# Revit family: 01546283
name_source: partatom
category: Plumbing Fixtures
revit_build: Autodesk Revit 2018 (Build: 20170223_1515(x64)
units: mm (PartAtom-declared; Revit-internal decimal feet)

## family parameters
Always vertical = Yes
Cut with Voids When Loaded = No
OmniClass Number = 23.45.55.00
OmniClass Title = Sanitary Faucets, Wastes
Part Type = Normal
Room Calculation Point = No
Round Connector Dimension = Use Diameter
Shared = No
Work Plane-Based = No

## types (1)
- 01546283 Washbasin faucet
    2D/3D/BIM Files URL = http://static.hansa.com
    3D View = https://static.hansa.com
    Advanced Features = Inner body made of DZR brass;Waterways without nickel coating
    Aerator = Laminar stream
    Approval ABP = PA-IX 29901/IA
    Approval KIWA = K6116/08
    AssetType = Fixed
    BIMObjectName = 01546283
    Backflow Prevention EN1717 = AA
    BodyMaterial = Brass
    Brand = HANSA
    Catalog Drawing URL = http://static.hansa.com
    Category = Health & Care
    CloseOffRating = 0
    Color = Chrome
    Connection = Eccentric coupling(s);Cover plate(s);with integrated shut-off valve(s);Silencer(s);Cover plate triple sealed
    Connection Size = G1/2
    Dimension Drawing URL = http://static.hansa.com
    DurationUnit = Year
    EAN Number = 4057304013133
    EN Standard = EN 817
    ETIM Class Number = EC011328 Washbasin mixing tap
    FDV Document URL = http://www.hansa.com
    FaucetMainMaterial = Brass
    Features = Single-lever
    Finish = Polished
    Flow Drawing URL = http://static.hansa.com
    Flow Rate At 300kPa With Flow Reducers = 0.2 L/s
    FlowCoefficient = 0
    Group = Washbasin faucet
    IfcExportAs = IfcValveType
    IfcExportType = FAUCET
    Installation Type = Wall mounted
    Installation Width = CC150± 15 mm
    Installation and Maintenance Guide URL = http://static.hansa.com
    Interactive AR View URL = https://static.hansa.com
    Lever Handle = Long shape;Hot/Cold symbols;Single operating lever/handle
    Long Marketing = HANSACLINICA wall-mounted washbasin faucet. Firm lever offers good usability to all users and situations. Swivel spout 120° (length=300 mm) with nickel-free waterways and laminar flow. The angle of swiveling can be limited to 60° or it can be locked. In-built limitation options for water temperature and maximum flow-rate. Includes three-time sealed cover plates.
    Manufacturer = HANSA
    ManufacturerName = HANSA
    ManufacturerURL = http://www.hansa.com
    Market = International;Germany;Austria;Belgium;Netherlands;France;Czech Republic;Slovakia;Italy;Spain
    Material = Brass
    Max. Hot Water Supply = 80 °C
    Mechanical Parts = Litter filter(s);ø 40 mm ceramic cartridge for flow and temperature control
    Mobile Product Information URL = http://mpi.hansa.com
    Model = 01546283 Washbasin faucet
    ModelReference = 01546283
    NBSDescription = Water supply fittings for wash basins and troughs
    NBSReference = 45-35-70/371
    Name = 01546283 Washbasin faucet
    Name_en = 01546283 Washbasin faucet
    Noise Class = I (ISO 3822)
    NominalDepth = 390 mm
    NominalHeight = 186 mm  [stored 0.610236 ft]
    NominalWidth = 215 mm
    Product Code = 01546283
    Product Family = HANSACLINICA
    Product Image URL = http://static.hansa.com
    Product URL = http://static.hansa.com
    Revision = 2
    Sales Package dimensions (LxWxH) = 345 x 218 x 202
    Shape = Sculptured
    Size = 215x390x185 mm
    Spare-Part Information URL = http://static.hansa.com
    Spout Projection = 377 mm
    Spout Swivel Range = 120° (60° / 0°)
    Spout Type = Swivel spout;Swivel range limiting option;Profile construction
    Surface treatment = Chrome
    Technical DataSheet URL = http://www.hansa.com
    Temperature = Temperature limiter;Temperature limiter (retrofittable)
    Temperature Adjustments = Limitation option for maximum temperature and flow-rate ;Adjustable hot water stop (included, retrofittable)
    UNSPSC Class Number = 30181700 Faucets or taps
    URL ABP = http://static.hansa.com
    URL Declaration of Conformity = http://static.hansa.com
    URL KIWA = http://static.hansa.com
    URL REACH = http://static.hansa.com
    Uniclass2 = Pr_40_30_96_96
    Uniclass2015Description = Washbasin manual water supply sets
    Uniclass2015Reference = Pr_40_20_87_96
    Version = 2
    VersionDate = 01/07/2022
    Warranty Information URL = http://warranty.hansa.com
    WarrantyDescription = http://warranty.hansa.com
    WarrantyDurationUnit = Year
    Working Pressure = 50 - 1000 kPa
    WorkingPressure = 50 - 1000 kPa

note: [stored X ft] marks values corroborated as IEEE doubles in the binary element streams (Revit-internal decimal feet)

## geometry (parser evidence)
native form markers: Sweep x5
no freeform markers — native parametric forms only
